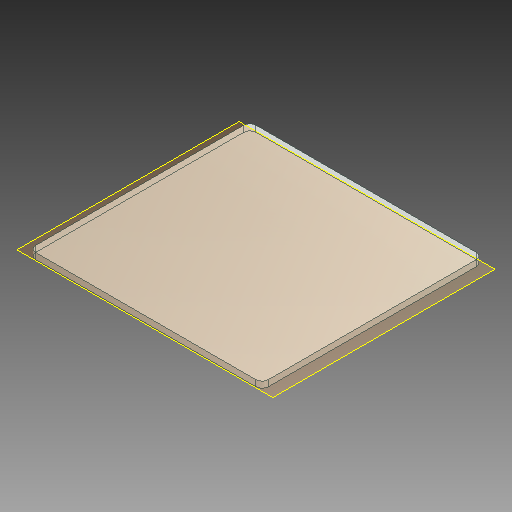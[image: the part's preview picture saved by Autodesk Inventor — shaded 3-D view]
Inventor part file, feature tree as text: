
AUTODESK INVENTOR PART (.ipt)
format: ipt  version: 2018 (Build 220112000, 112)  size: 112,640 bytes
history: native  units: mm
features: other x3, plane x1, extrude x1, sketch x1, reference x1
ambient origin geometry x8: Origin, YZ Plane, XZ Plane, XY Plane, X Axis, Y Axis, Z Axis, Center Point
bodies: Volumenkörper1 (feature_tree)
feature tree (7):
  plane  "Arbeitsebene1"
  extrude  "Extrusion1"  Depth=10.0mm TaperAngle=0.0deg
  sketch  "Skizze1"  dims[d0=10.0mm d1=10.0mm d2=0.0mm]
  reference  "Referenz1"
  parser-record x1  (decoder bookkeeping rows leaked as tree rows — omitted from the tree; the rows remain in map.json)
  other  "SmartCube.iam"
  other  "SitzFläche:1"
note: 1 file-system path scrubbed to <path> (originals preserved in map.json)
